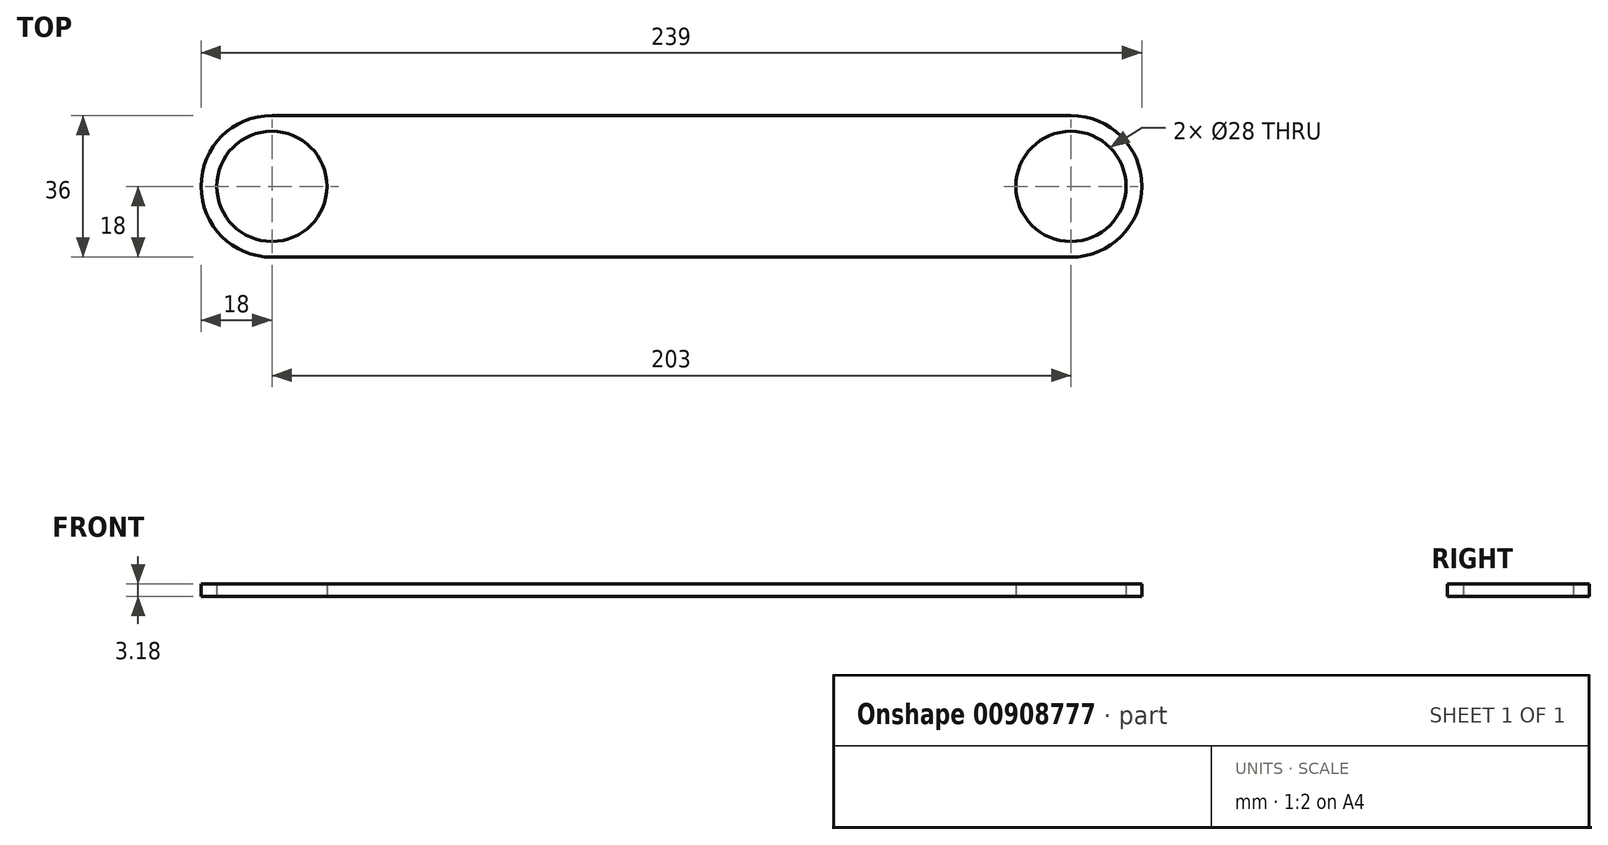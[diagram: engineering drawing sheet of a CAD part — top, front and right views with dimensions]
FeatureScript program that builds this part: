
annotation { "Feature Type Name" : "Feature", "Feature Type Description" : "" }
export const myFeature = defineFeature(function(context is Context, id is Id, definition is map)
    precondition{}
    {
        {
            var Q0;
            Q0=qCreatedBy(makeId("Top.planeOp"),FACE);
            var sketch = newSketch(context, id + "F0", { "sketchPlane" : qUnion([Q0])});
            skPoint(sketch, "E0.middle", {"position": v(0, 0) * mm});
            skLineSegment(sketch, "E1.bottom", {"start": v(87.5, 18) * mm, "end": v(-87.5, 18) * mm});
            skLineSegment(sketch, "E1.top", {"start": v(87.5, -18) * mm, "end": v(-87.5, -18) * mm});
            skLineSegment(sketch, "E1.left", {"start": v(87.5, 18) * mm, "end": v(87.5, -18) * mm, "construction": true});
            skLineSegment(sketch, "E1.right", {"start": v(-87.5, 18) * mm, "end": v(-87.5, -18) * mm, "construction": true});
            skLineSegment(sketch, "E2", {"start": v(87.5, 0) * mm, "end": v(101.5, 0) * mm});
            skLineSegment(sketch, "E3", {"start": v(-87.5, 0) * mm, "end": v(-101.5, 0) * mm});
            skCircle(sketch, "E4", {"center": v(-101.5, 0) * mm, "radius": 14 * mm});
            skCircle(sketch, "E5", {"center": v(101.5, 0) * mm, "radius": 14 * mm});
            skLineSegment(sketch, "E6", {"start": v(87.5, -18) * mm, "end": v(101.5, -18) * mm});
            skArc(sketch, "E7", {"start": v(101.5, -18) * mm, "mid": v(119.5, 0) * mm, "end": v(101.5, 18) * mm});
            skLineSegment(sketch, "E8", {"start": v(0, -18) * mm, "end": v(0, 18) * mm, "construction": true});
            skArc(sketch, "E9.MirrorC", {"start": v(-101.5, -18) * mm, "mid": v(-119.5, 0) * mm, "end": v(-101.5, 18) * mm});
            skLineSegment(sketch, "E10", {"start": v(-87.5, 18) * mm, "end": v(-101.5, 18) * mm});
            skLineSegment(sketch, "E11", {"start": v(-87.5, -18) * mm, "end": v(-101.5, -18) * mm});
            skLineSegment(sketch, "E12", {"start": v(87.5, 18) * mm, "end": v(101.5, 18) * mm});
            skSolve(sketch);
        }
        {
            var Q0;
            Q0 = qSketchRegion(id + "F0", true);
            extrude(context, id + "F1", {"entities" : qUnion([Q0]), "depth" : 3.17 * mm, "offsetDistance" : 25.4 * mm});
        }
    });
